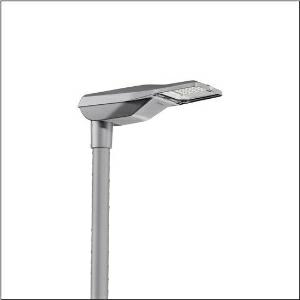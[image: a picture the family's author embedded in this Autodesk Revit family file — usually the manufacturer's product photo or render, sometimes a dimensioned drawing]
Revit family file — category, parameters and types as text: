
# Revit family: streetlight_sl_21_iq_micro___st0_8a_5xe1c21g08cb_23b1
name_source: partatom
category: Lighting Fixtures
units: mm (PartAtom-declared; Revit-internal decimal feet)

## family parameters
Cut with Voids When Loaded = No
Host = Face
Light Source = No
Part Type = Normal
Room Calculation Point = No
Round Connector Dimension = Use Diameter
Shared = No

## types (1)
- --- (1 x LED, 2380 lm, 19.4 W, 2200K)
    Apparent Load = 19 VA
    CIE Flux Codes = 38 75 97 100 100
    Color Rendering = 70
    Color Temperature = 2200K
    Default Elevation = 1800 mm
    Description = Streetlight SL 21 iQ micro, mast luminaire, primary light control with lens, of PMMA, primary optical cover: cover, of toughened safety glass, transparent, light distribution: ST0.8a, light emission: direct distribution, primary light characteristic: asymmetric, installation type: post-top, side-entry, LED, High Power LED, rated luminous flux: 2.380lm, luminous efficacy: 123lm/W, light colour: 722, colour temperature: 2200K, control gear: iQ Street-Remote, control: Street-Remote, Auto-Match, Temp-Guard, Lumen-Switch, Night-Set, Smart-Wire, Light-Fading, Desk-Remote (wireless, voltage-free reading and setting of iQ features in the workshop via application-optimized NFC function/RFID function), optimised constant luminous flux control (CLO 2.0), pre-setting: linear dimming characteristic, mains connection: 220..240V, AC, 50/60Hz, start of lifetime: 19W, end of service life: 20W, reduction: 10W, luminaire housing, of diecast aluminium, powder-coated, Siteco® metallic grey (DB 702S), corrosivity category C5 mid according to DIN EN ISO 12944, please order mast flange separately, inclination adjustable: 0°, 5°, 10°, 15°, sealing non-destructively replaceable, multi-level sealing system, length: 528mm, width: 235mm, height: 110mm, mast flange for spigot size: 42mm (side-entry): 5XC10008XM4, 60/48mm (side-entry/post-top): 5XC10108XM2, 76/60mm (side-entry/post-top): 5XC10108XM1, protection rating (complete): IP66, insulation class (complete): insulation class II (safety insulation), certification: CE, ENEC, ENEC+, VDE, impact resistance: IK10, permissible operating ambient temperature for outdoor applications: -40..+50°C, standard-compliant lighting for roads and squares, packaging unit: 1 piece

Light Distribution: ST0.8a
    Height = 110 mm
    Lamp = 1 x LED
    Lamp Light Flux = 2380 lm
    Lamp Power = 19.4 W
    Lamp count = 1
    Length = 528 mm
    Luminous efficacy = 123 lm/W
    Manufacturer = Siteco
    ModVariant = No
    Model = 5XE1C21G08CB
    Number of Poles = 1
    OnlyDefault = Yes
    Power Factor = 1
    Product Name = Streetlight SL 21 iQ micro | ST0.8a
    Product group = mast luminaire | pylon top
    ProductGroupID = 6100
    Protection Class = Protection class II
    Protection Degree = IP 66
    RLX_Detail_Level = 1
    RLX_Emergency_Light_Flux = 0 lm
    RLX_Emergency_Type = 0
    RLX_Emergency_Type_DB = No
    RlxData = <blob elided: 98677 chars, md5=e92cdc77>
    Socket = socket
    Standby Power = 0 W
    System Light Flux = 2380 lm
    System Power = 19 W
    Type Comments = factory setting: luminous flux: 100 % | dim-lin: 254 | 387 mA
    Type Image = l_1006881.jpg
    URL = http://relux.com
    VarID = @adj_138500
    Voltage = 0 V
    Weight = 0.00 kg
    Width = 235 mm

## geometry (parser evidence)
native form markers: Blend x4, Sweep x12
no freeform markers — native parametric forms only
